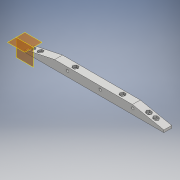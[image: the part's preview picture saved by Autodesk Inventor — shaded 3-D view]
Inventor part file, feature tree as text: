
AUTODESK INVENTOR PART (.ipt)
format: ipt  version: 2017 (Build 210142000, 142)  size: 216,576 bytes
history: native  units: mm
features: sketch x9, extrude x9, plane x7
ambient origin geometry x8: Origin, YZ Plane, XZ Plane, XY Plane, X Axis, Y Axis, Z Axis, Center Point
bodies: Solid1 (feature_tree)
feature tree (25):
  sketch  "Sketch1"  dims[d1=10.0mm d2=90.0deg]
  plane  "Work Plane2"
  sketch  "Sketch2"  dims[d4=3.2mm d6=3.2mm]
  plane  "Work Plane1"
  extrude  "klocek"  TaperAngle=90.0deg  [1 undecoded]
  plane  "Work Plane3"
  extrude  "prowadzenie osi"  Depth=3.2mm
  plane  "Work Plane4"
  sketch  "Sketch7"  dims[d9=42.5mm d13=3.2mm]
  sketch  "Sketch8"  dims[d15=3.2mm d16=83.0mm]
  extrude  "przedni skos"  Depth=60.0mm
  extrude  "tylni skos"  Depth=3.2mm
  plane  "Work Plane7"
  sketch  "Sketch5"  dims[d7=3.2mm d8=60.0mm]
  extrude  "hex insert middle"  Depth=83.0mm
  plane  "Work Plane6"
  sketch  "Sketch9"  dims[d17=3.2mm d18=41.5mm]
  extrude  "hex insert rear 1"  Depth=41.5mm
  plane  "Work Plane5"
  extrude  "hex insert rear 2"  Depth=3.2mm
  extrude  "Extrusion18"  Depth=15.0mm
  extrude  "Extrusion19"  Depth=5.9mm
  sketch  "Sketch10"  dims[d26=3.2mm d27=33.5mm d28=3.2mm d29=44.5mm]
  sketch  "Sketch13"  dims[d32=15.0mm d33=15.0mm]
  sketch  "Sketch16"  dims[d38=11.0mm d39=0.0mm d44=5.9mm d45=5.9mm d51=5.9mm d61=3.2mm d62=10.0mm d63=9.0mm d64=54.5mm d65=41.5mm d67=11.0mm d68=0.0mm d70=6.0mm d71=0.0mm d72=5.9mm d77=5.0mm d78=0.0mm d80=8.0mm d81=40.0mm d82=3.0mm d83=0.0mm d84=7.5mm d85=0.0mm d86=8.0mm d87=38.0mm d88=7.0mm d89=0.0mm d90=5.9mm d91=9.0mm d92=0.0mm d93=5.9mm d94=7.5mm d95=0.0mm]
note: 1 required parameter value undecoded (feature->parameter linkage not recoverable at this tier; creation-order binding heuristic only, values carry confidence <= 0.55)
